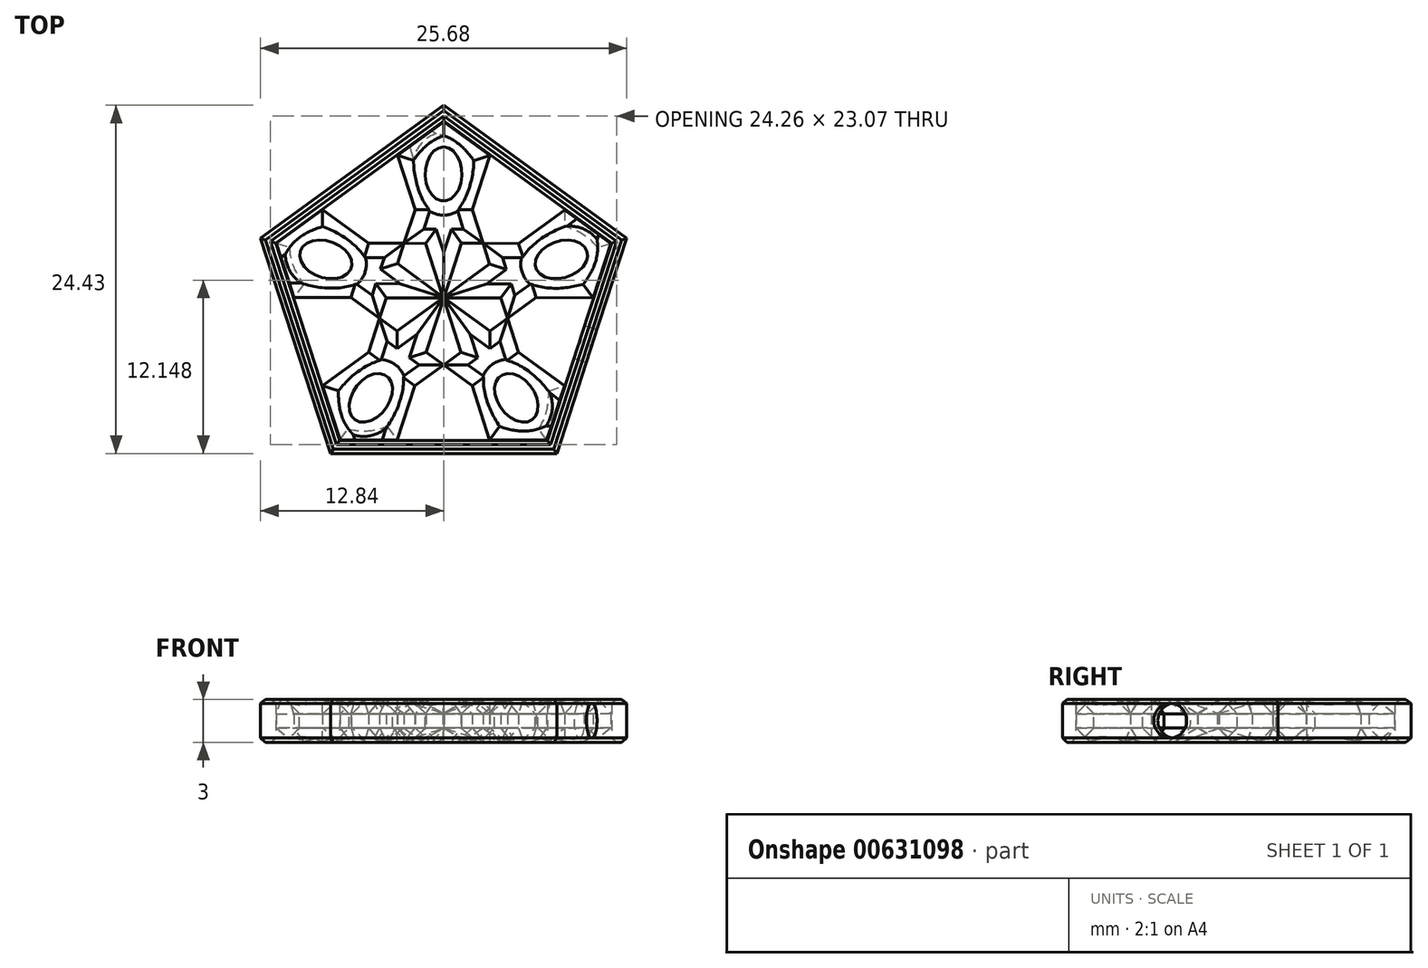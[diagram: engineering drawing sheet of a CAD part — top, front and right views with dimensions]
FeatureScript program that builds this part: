
annotation { "Feature Type Name" : "Feature", "Feature Type Description" : "" }
export const myFeature = defineFeature(function(context is Context, id is Id, definition is map)
    precondition{}
    {
        {
            var Q0;
            Q0=qCreatedBy(makeId("Top.planeOp"),FACE);
            var sketch = newSketch(context, id + "F0", { "sketchPlane" : qUnion([Q0])});
            skCircle(sketch, "E0.cCircle", {"center": v(0, 3.43) * mm, "radius": 2.75 * mm, "construction": true});
            skLineSegment(sketch, "E0.0", {"start": v(-2, 6.18) * mm, "end": v(2, 6.17) * mm});
            skLineSegment(sketch, "E0.1", {"start": v(2, 6.17) * mm, "end": v(3.23, 2.37) * mm});
            skLineSegment(sketch, "E0.2", {"start": v(3.23, 2.37) * mm, "end": v(0, 0.02) * mm});
            skLineSegment(sketch, "E0.3", {"start": v(0, 0.02) * mm, "end": v(-3.24, 2.38) * mm});
            skLineSegment(sketch, "E0.4", {"start": v(-3.24, 2.38) * mm, "end": v(-2, 6.18) * mm});
            skPoint(sketch, "E0.0.midPoint", {"position": v(0, 6.18) * mm});
            skLineSegment(sketch, "E1.MirrorCS", {"start": v(-3.22, 9.99) * mm, "end": v(-2, 6.18) * mm});
            skLineSegment(sketch, "E2.MirrorCS", {"start": v(0.02, 12.33) * mm, "end": v(-3.22, 9.99) * mm});
            skLineSegment(sketch, "E3.MirrorCS", {"start": v(3.25, 9.98) * mm, "end": v(0.02, 12.33) * mm});
            skLineSegment(sketch, "E4.MirrorCS", {"start": v(2, 6.17) * mm, "end": v(3.25, 9.98) * mm});
            skLineSegment(sketch, "E5.1.0", {"start": v(-6.5, 0.01) * mm, "end": v(-5.25, 3.82) * mm});
            skCircle(sketch, "E5.1.1", {"center": v(-3.26, 1.06) * mm, "radius": 2.75 * mm, "construction": true});
            skLineSegment(sketch, "E5.1.2", {"start": v(-5.25, 3.82) * mm, "end": v(-8.48, 6.17) * mm});
            skLineSegment(sketch, "E5.1.3", {"start": v(-11.73, 3.83) * mm, "end": v(-10.5, 0.02) * mm});
            skLineSegment(sketch, "E5.1.4", {"start": v(-3.26, -2.34) * mm, "end": v(-6.5, 0.01) * mm});
            skLineSegment(sketch, "E5.1.5", {"start": v(-0.02, 0) * mm, "end": v(-3.26, -2.34) * mm});
            skLineSegment(sketch, "E5.1.6", {"start": v(-8.48, 6.17) * mm, "end": v(-11.73, 3.83) * mm});
            skLineSegment(sketch, "E5.1.7", {"start": v(-11.73, 3.83) * mm, "end": v(-10.5, 0.02) * mm});
            skLineSegment(sketch, "E5.1.8", {"start": v(-1.25, 3.8) * mm, "end": v(-0.02, 0) * mm});
            skPoint(sketch, "E5.1.9", {"position": v(-5.87, 1.91) * mm});
            skLineSegment(sketch, "E5.1.10", {"start": v(-5.25, 3.82) * mm, "end": v(-1.25, 3.8) * mm});
            skLineSegment(sketch, "E5.1.11", {"start": v(-10.5, 0.02) * mm, "end": v(-6.5, 0.01) * mm});
            skLineSegment(sketch, "E5.2.0", {"start": v(-2.02, -6.17) * mm, "end": v(-5.25, -3.82) * mm});
            skCircle(sketch, "E5.2.1", {"center": v(-2.01, -2.77) * mm, "radius": 2.75 * mm, "construction": true});
            skLineSegment(sketch, "E5.2.2", {"start": v(-5.25, -3.82) * mm, "end": v(-8.5, -6.16) * mm});
            skLineSegment(sketch, "E5.2.3", {"start": v(-7.26, -9.97) * mm, "end": v(-3.26, -9.98) * mm});
            skLineSegment(sketch, "E5.2.4", {"start": v(1.22, -3.83) * mm, "end": v(-2.02, -6.17) * mm});
            skLineSegment(sketch, "E5.2.5", {"start": v(0, -0.02) * mm, "end": v(1.22, -3.83) * mm});
            skLineSegment(sketch, "E5.2.6", {"start": v(-8.5, -6.16) * mm, "end": v(-7.26, -9.97) * mm});
            skLineSegment(sketch, "E5.2.7", {"start": v(-7.26, -9.97) * mm, "end": v(-3.26, -9.98) * mm});
            skLineSegment(sketch, "E5.2.8", {"start": v(-4, -0.02) * mm, "end": v(0, -0.02) * mm});
            skPoint(sketch, "E5.2.9", {"position": v(-3.64, -5) * mm});
            skLineSegment(sketch, "E5.2.10", {"start": v(-5.25, -3.82) * mm, "end": v(-4, -0.02) * mm});
            skLineSegment(sketch, "E5.2.11", {"start": v(-3.26, -9.98) * mm, "end": v(-2.02, -6.17) * mm});
            skLineSegment(sketch, "E5.3.0", {"start": v(5.25, -3.83) * mm, "end": v(2, -6.17) * mm});
            skCircle(sketch, "E5.3.1", {"center": v(2.01, -2.77) * mm, "radius": 2.75 * mm, "construction": true});
            skLineSegment(sketch, "E5.3.2", {"start": v(2, -6.17) * mm, "end": v(3.24, -9.98) * mm});
            skLineSegment(sketch, "E5.3.3", {"start": v(7.24, -9.99) * mm, "end": v(8.48, -6.19) * mm});
            skLineSegment(sketch, "E5.3.4", {"start": v(4.02, -0.02) * mm, "end": v(5.25, -3.83) * mm});
            skLineSegment(sketch, "E5.3.5", {"start": v(0.02, -0.02) * mm, "end": v(4.02, -0.02) * mm});
            skLineSegment(sketch, "E5.3.6", {"start": v(3.24, -9.98) * mm, "end": v(7.24, -9.99) * mm});
            skLineSegment(sketch, "E5.3.7", {"start": v(7.24, -9.99) * mm, "end": v(8.48, -6.19) * mm});
            skLineSegment(sketch, "E5.3.8", {"start": v(-1.22, -3.82) * mm, "end": v(0.02, -0.02) * mm});
            skPoint(sketch, "E5.3.9", {"position": v(3.63, -5) * mm});
            skLineSegment(sketch, "E5.3.10", {"start": v(2, -6.17) * mm, "end": v(-1.22, -3.82) * mm});
            skLineSegment(sketch, "E5.3.11", {"start": v(8.48, -6.19) * mm, "end": v(5.25, -3.83) * mm});
            skLineSegment(sketch, "E5.4.0", {"start": v(5.26, 3.8) * mm, "end": v(6.5, 0) * mm});
            skCircle(sketch, "E5.4.1", {"center": v(3.26, 1.06) * mm, "radius": 2.75 * mm, "construction": true});
            skLineSegment(sketch, "E5.4.2", {"start": v(6.5, 0) * mm, "end": v(10.5, 0) * mm});
            skLineSegment(sketch, "E5.4.3", {"start": v(11.74, 3.8) * mm, "end": v(8.5, 6.15) * mm});
            skLineSegment(sketch, "E5.4.4", {"start": v(1.26, 3.82) * mm, "end": v(5.26, 3.8) * mm});
            skLineSegment(sketch, "E5.4.5", {"start": v(0.02, 0.01) * mm, "end": v(1.26, 3.82) * mm});
            skLineSegment(sketch, "E5.4.6", {"start": v(10.5, 0) * mm, "end": v(11.74, 3.8) * mm});
            skLineSegment(sketch, "E5.4.7", {"start": v(11.74, 3.8) * mm, "end": v(8.5, 6.15) * mm});
            skLineSegment(sketch, "E5.4.8", {"start": v(3.25, -2.34) * mm, "end": v(0.02, 0.01) * mm});
            skPoint(sketch, "E5.4.9", {"position": v(5.88, 1.9) * mm});
            skLineSegment(sketch, "E5.4.10", {"start": v(6.5, 0) * mm, "end": v(3.25, -2.34) * mm});
            skLineSegment(sketch, "E5.4.11", {"start": v(8.5, 6.15) * mm, "end": v(5.26, 3.8) * mm});
            skPoint(sketch, "E5.center", {"position": v(0, 0) * mm});
            skEllipse(sketch, "E6", {"center": v(0, 8.68) * mm, "majorRadius": 1.9 * mm, "minorRadius": 1.29 * mm, "majorAxis": v(0, 1)});
            skEllipse(sketch, "E7.1.1", {"center": v(-8.26, 2.68) * mm, "majorRadius": 1.9 * mm, "minorRadius": 1.29 * mm, "majorAxis": v(-0.95, 0.3)});
            skEllipse(sketch, "E7.2.1", {"center": v(-5.1, -7.02) * mm, "majorRadius": 1.9 * mm, "minorRadius": 1.29 * mm, "majorAxis": v(-0.59, -0.8)});
            skEllipse(sketch, "E7.3.1", {"center": v(5.1, -7.02) * mm, "majorRadius": 1.9 * mm, "minorRadius": 1.29 * mm, "majorAxis": v(0.59, -0.8)});
            skEllipse(sketch, "E7.4.1", {"center": v(8.26, 2.68) * mm, "majorRadius": 1.9 * mm, "minorRadius": 1.29 * mm, "majorAxis": v(0.95, 0.3)});
            skSolve(sketch);
        }
        {
            var Q0;
            {var subQ6=sQuery(id+"F0.wireOp",EDGE,"E0.0");Q0=makeQuery(id+"F0.imprint","IMPRINT",FACE,{"disambiguationData":[TD([[makeQuery(id+"F0.imprint","IMPRINT",EDGE,{"derivedFrom":subQ6}),-1.0]])]});}
            var Q1;
            Q1=makeQuery(id+"F0.imprint","IMPRINT",FACE,{"disambiguationData":[TD([[makeQuery(id+"F0.imprint","IMPRINT",EDGE,{"derivedFrom":sQuery(id+"F0.wireOp",EDGE,"E0.0")}),1.0]])]});
            extrude(context, id + "F1", {"entities" : qUnion([Q0, Q1]), "depth" : 3 * mm, "offsetDistance" : 25 * mm});
        }
        {
            var Q0;
            Q0=makeQuery(id+"F1.opExtrude","CAP_EDGE",EDGE,{"disambiguationData":[OSD([sQuery(id+"F0.wireOp",EDGE,"E5.1.8")])],"isStart":false});
            var Q1;
            Q1=makeQuery(id+"F1.opExtrude","CAP_EDGE",EDGE,{"disambiguationData":[OSD([sQuery(id+"F0.wireOp",EDGE,"E5.1.10")])],"isStart":false});
            var Q2;
            Q2=makeQuery(id+"F1.opExtrude","CAP_EDGE",EDGE,{"disambiguationData":[OSD([sQuery(id+"F0.wireOp",EDGE,"E0.4")])],"isStart":false});
            var Q3;
            Q3=makeQuery(id+"F1.opExtrude","CAP_EDGE",EDGE,{"disambiguationData":[OSD([sQuery(id+"F0.wireOp",EDGE,"E1.MirrorCS")])],"isStart":false});
            var Q4;
            Q4=makeQuery(id+"F1.opExtrude","CAP_EDGE",EDGE,{"disambiguationData":[OSD([sQuery(id+"F0.wireOp",EDGE,"E2.MirrorCS")])],"isStart":false});
            var Q5;
            Q5=makeQuery(id+"F1.opExtrude","CAP_EDGE",EDGE,{"disambiguationData":[OSD([sQuery(id+"F0.wireOp",EDGE,"E3.MirrorCS")])],"isStart":false});
            var Q6;
            Q6=makeQuery(id+"F1.opExtrude","CAP_EDGE",EDGE,{"disambiguationData":[OSD([sQuery(id+"F0.wireOp",EDGE,"E4.MirrorCS")])],"isStart":false});
            var Q7;
            Q7=makeQuery(id+"F1.opExtrude","CAP_EDGE",EDGE,{"disambiguationData":[OSD([sQuery(id+"F0.wireOp",EDGE,"E0.1")])],"isStart":false});
            var Q8;
            Q8=makeQuery(id+"F1.opExtrude","CAP_EDGE",EDGE,{"disambiguationData":[OSD([sQuery(id+"F0.wireOp",EDGE,"E5.4.4")])],"isStart":false});
            var Q9;
            Q9=makeQuery(id+"F1.opExtrude","CAP_FACE",FACE,{"disambiguationData":[OSD([sQuery(id+"F0.wireOp",EDGE,"E0.1"),sQuery(id+"F0.wireOp",EDGE,"E0.2"),sQuery(id+"F0.wireOp",EDGE,"E0.3"),sQuery(id+"F0.wireOp",EDGE,"E0.4"),sQuery(id+"F0.wireOp",EDGE,"E1.MirrorCS"),sQuery(id+"F0.wireOp",EDGE,"E2.MirrorCS"),sQuery(id+"F0.wireOp",EDGE,"E3.MirrorCS"),sQuery(id+"F0.wireOp",EDGE,"E4.MirrorCS"),sQuery(id+"F0.wireOp",EDGE,"E5.1.8"),sQuery(id+"F0.wireOp",EDGE,"E5.1.10"),sQuery(id+"F0.wireOp",EDGE,"E5.4.4"),sQuery(id+"F0.wireOp",EDGE,"E5.4.5"),sQuery(id+"F0.wireOp",EDGE,"E6")])],"isStart":false});
            chamfer(context, id + "F2", {"entities" : qUnion([Q0, Q1, Q2, Q3, Q4, Q5, Q6, Q7, Q8, Q9]), "width" : 1 * mm, "tangentPropagation" : true});
        }
        {
            var Q0;
            Q0=makeQuery(id+"F0.imprint","IMPRINT",FACE,{"disambiguationData":[TD([[makeQuery(id+"F0.imprint","IMPRINT",EDGE,{"derivedFrom":sQuery(id+"F0.wireOp",EDGE,"E5.4.0")}),1.0]])]});
            var Q1;
            {var subQ6=sQuery(id+"F0.wireOp",EDGE,"E5.4.0");Q1=makeQuery(id+"F0.imprint","IMPRINT",FACE,{"disambiguationData":[TD([[makeQuery(id+"F0.imprint","IMPRINT",EDGE,{"derivedFrom":subQ6}),-1.0]])]});}
            extrude(context, id + "F3", {"entities" : qUnion([Q0, Q1]), "depth" : 3 * mm, "offsetDistance" : 25 * mm});
        }
        {
            var Q0;
            Q0=makeQuery(id+"F3.opExtrude","CAP_EDGE",EDGE,{"disambiguationData":[OSD([sQuery(id+"F0.wireOp",EDGE,"E5.3.5")])],"isStart":false});
            var Q1;
            Q1=makeQuery(id+"F3.opExtrude","CAP_EDGE",EDGE,{"disambiguationData":[OSD([sQuery(id+"F0.wireOp",EDGE,"E0.2")])],"isStart":false});
            var Q2;
            Q2=makeQuery(id+"F3.opExtrude","CAP_EDGE",EDGE,{"disambiguationData":[OSD([sQuery(id+"F0.wireOp",EDGE,"E0.1")])],"isStart":false});
            var Q3;
            Q3=makeQuery(id+"F3.opExtrude","CAP_EDGE",EDGE,{"disambiguationData":[OSD([sQuery(id+"F0.wireOp",EDGE,"E5.4.4")])],"isStart":false});
            var Q4;
            Q4=makeQuery(id+"F3.opExtrude","CAP_EDGE",EDGE,{"disambiguationData":[OSD([sQuery(id+"F0.wireOp",EDGE,"E5.4.11")])],"isStart":false});
            var Q5;
            Q5=makeQuery(id+"F3.opExtrude","CAP_EDGE",EDGE,{"disambiguationData":[OSD([sQuery(id+"F0.wireOp",EDGE,"E5.4.3")])],"isStart":false});
            var Q6;
            Q6=makeQuery(id+"F3.opExtrude","CAP_EDGE",EDGE,{"disambiguationData":[OSD([sQuery(id+"F0.wireOp",EDGE,"E5.4.10")])],"isStart":false});
            var Q7;
            Q7=makeQuery(id+"F3.opExtrude","CAP_EDGE",EDGE,{"disambiguationData":[OSD([sQuery(id+"F0.wireOp",EDGE,"E5.3.4")])],"isStart":false});
            var Q8;
            Q8=makeQuery(id+"F3.opExtrude","CAP_EDGE",EDGE,{"disambiguationData":[OSD([sQuery(id+"F0.wireOp",EDGE,"E5.4.2")])],"isStart":false});
            var Q9;
            Q9=makeQuery(id+"F3.opExtrude","CAP_EDGE",EDGE,{"disambiguationData":[OSD([sQuery(id+"F0.wireOp",EDGE,"E5.4.6")])],"isStart":false});
            var Q10;
            Q10=makeQuery(id+"F3.opExtrude","CAP_EDGE",EDGE,{"disambiguationData":[OSD([sQuery(id+"F0.wireOp",EDGE,"E7.4.1")])],"isStart":false});
            chamfer(context, id + "F4", {"entities" : qUnion([Q0, Q1, Q2, Q3, Q4, Q5, Q6, Q7, Q8, Q9, Q10]), "width" : 1 * mm, "tangentPropagation" : true});
        }
        {
            var Q0;
            {var subQ1=sQuery(id+"F0.wireOp",EDGE,"E5.3.0");Q0=makeQuery(id+"F0.imprint","IMPRINT",FACE,{"disambiguationData":[TD([[makeQuery(id+"F0.imprint","IMPRINT",EDGE,{"derivedFrom":subQ1}),-1.0]])]});}
            var Q1;
            Q1=makeQuery(id+"F0.imprint","IMPRINT",FACE,{"disambiguationData":[TD([[makeQuery(id+"F0.imprint","IMPRINT",EDGE,{"derivedFrom":sQuery(id+"F0.wireOp",EDGE,"E5.3.0")}),1.0]])]});
            extrude(context, id + "F5", {"entities" : qUnion([Q0, Q1]), "depth" : 3 * mm, "offsetDistance" : 25 * mm});
        }
        {
            var Q0;
            {var subQ1=sQuery(id+"F0.wireOp",EDGE,"E5.2.0");Q0=makeQuery(id+"F0.imprint","IMPRINT",FACE,{"disambiguationData":[TD([[makeQuery(id+"F0.imprint","IMPRINT",EDGE,{"derivedFrom":subQ1}),-1.0]])]});}
            var Q1;
            Q1=makeQuery(id+"F0.imprint","IMPRINT",FACE,{"disambiguationData":[TD([[makeQuery(id+"F0.imprint","IMPRINT",EDGE,{"derivedFrom":sQuery(id+"F0.wireOp",EDGE,"E5.2.0")}),1.0]])]});
            extrude(context, id + "F6", {"entities" : qUnion([Q0, Q1]), "depth" : 3 * mm, "offsetDistance" : 25 * mm});
        }
        {
            var Q0;
            {var subQ1=sQuery(id+"F0.wireOp",EDGE,"E5.1.0");Q0=makeQuery(id+"F0.imprint","IMPRINT",FACE,{"disambiguationData":[TD([[makeQuery(id+"F0.imprint","IMPRINT",EDGE,{"derivedFrom":subQ1}),-1.0]])]});}
            var Q1;
            Q1=makeQuery(id+"F0.imprint","IMPRINT",FACE,{"disambiguationData":[TD([[makeQuery(id+"F0.imprint","IMPRINT",EDGE,{"derivedFrom":sQuery(id+"F0.wireOp",EDGE,"E5.1.0")}),1.0]])]});
            extrude(context, id + "F7", {"entities" : qUnion([Q0, Q1]), "depth" : 3 * mm, "offsetDistance" : 25 * mm});
        }
        {
            var Q0;
            Q0=makeQuery(id+"F5.opExtrude","CAP_EDGE",EDGE,{"disambiguationData":[OSD([sQuery(id+"F0.wireOp",EDGE,"E5.4.8")])],"isStart":false});
            var Q1;
            Q1=makeQuery(id+"F5.opExtrude","CAP_EDGE",EDGE,{"disambiguationData":[OSD([sQuery(id+"F0.wireOp",EDGE,"E5.4.10")])],"isStart":false});
            var Q2;
            Q2=makeQuery(id+"F5.opExtrude","CAP_EDGE",EDGE,{"disambiguationData":[OSD([sQuery(id+"F0.wireOp",EDGE,"E5.3.4")])],"isStart":false});
            var Q3;
            Q3=makeQuery(id+"F5.opExtrude","CAP_EDGE",EDGE,{"disambiguationData":[OSD([sQuery(id+"F0.wireOp",EDGE,"E5.3.11")])],"isStart":false});
            var Q4;
            Q4=makeQuery(id+"F5.opExtrude","CAP_EDGE",EDGE,{"disambiguationData":[OSD([sQuery(id+"F0.wireOp",EDGE,"E5.3.7")])],"isStart":false});
            var Q5;
            Q5=makeQuery(id+"F5.opExtrude","CAP_EDGE",EDGE,{"disambiguationData":[OSD([sQuery(id+"F0.wireOp",EDGE,"E5.3.6")])],"isStart":false});
            var Q6;
            Q6=makeQuery(id+"F5.opExtrude","CAP_EDGE",EDGE,{"disambiguationData":[OSD([sQuery(id+"F0.wireOp",EDGE,"E5.3.2")])],"isStart":false});
            var Q7;
            Q7=makeQuery(id+"F5.opExtrude","CAP_EDGE",EDGE,{"disambiguationData":[OSD([sQuery(id+"F0.wireOp",EDGE,"E5.3.10")])],"isStart":false});
            var Q8;
            Q8=makeQuery(id+"F5.opExtrude","CAP_EDGE",EDGE,{"disambiguationData":[OSD([sQuery(id+"F0.wireOp",EDGE,"E5.2.4")])],"isStart":false});
            var Q9;
            Q9=makeQuery(id+"F5.opExtrude","CAP_EDGE",EDGE,{"disambiguationData":[OSD([sQuery(id+"F0.wireOp",EDGE,"E5.2.5")])],"isStart":false});
            var Q10;
            Q10=makeQuery(id+"F5.opExtrude","CAP_EDGE",EDGE,{"disambiguationData":[OSD([sQuery(id+"F0.wireOp",EDGE,"E7.3.1")])],"isStart":false});
            chamfer(context, id + "F8", {"entities" : qUnion([Q0, Q1, Q2, Q3, Q4, Q5, Q6, Q7, Q8, Q9, Q10]), "width" : 1 * mm, "tangentPropagation" : true});
        }
        {
            var Q0;
            Q0=makeQuery(id+"F6.opExtrude","CAP_EDGE",EDGE,{"disambiguationData":[OSD([sQuery(id+"F0.wireOp",EDGE,"E7.2.1")])],"isStart":false});
            var Q1;
            Q1=makeQuery(id+"F6.opExtrude","CAP_EDGE",EDGE,{"disambiguationData":[OSD([sQuery(id+"F0.wireOp",EDGE,"E5.2.3")])],"isStart":false});
            var Q2;
            Q2=makeQuery(id+"F6.opExtrude","CAP_EDGE",EDGE,{"disambiguationData":[OSD([sQuery(id+"F0.wireOp",EDGE,"E5.2.6")])],"isStart":false});
            var Q3;
            Q3=makeQuery(id+"F6.opExtrude","CAP_EDGE",EDGE,{"disambiguationData":[OSD([sQuery(id+"F0.wireOp",EDGE,"E5.2.2")])],"isStart":false});
            var Q4;
            Q4=makeQuery(id+"F6.opExtrude","CAP_EDGE",EDGE,{"disambiguationData":[OSD([sQuery(id+"F0.wireOp",EDGE,"E5.2.10")])],"isStart":false});
            var Q5;
            Q5=makeQuery(id+"F6.opExtrude","CAP_EDGE",EDGE,{"disambiguationData":[OSD([sQuery(id+"F0.wireOp",EDGE,"E5.1.4")])],"isStart":false});
            var Q6;
            Q6=makeQuery(id+"F6.opExtrude","CAP_EDGE",EDGE,{"disambiguationData":[OSD([sQuery(id+"F0.wireOp",EDGE,"E5.1.5")])],"isStart":false});
            var Q7;
            Q7=makeQuery(id+"F6.opExtrude","CAP_EDGE",EDGE,{"disambiguationData":[OSD([sQuery(id+"F0.wireOp",EDGE,"E5.3.8")])],"isStart":false});
            var Q8;
            Q8=makeQuery(id+"F6.opExtrude","CAP_EDGE",EDGE,{"disambiguationData":[OSD([sQuery(id+"F0.wireOp",EDGE,"E5.3.10")])],"isStart":false});
            var Q9;
            Q9=makeQuery(id+"F6.opExtrude","CAP_EDGE",EDGE,{"disambiguationData":[OSD([sQuery(id+"F0.wireOp",EDGE,"E5.2.4")])],"isStart":false});
            var Q10;
            Q10=makeQuery(id+"F6.opExtrude","CAP_EDGE",EDGE,{"disambiguationData":[OSD([sQuery(id+"F0.wireOp",EDGE,"E5.2.11")])],"isStart":false});
            chamfer(context, id + "F9", {"entities" : qUnion([Q0, Q1, Q2, Q3, Q4, Q5, Q6, Q7, Q8, Q9, Q10]), "width" : 1 * mm, "tangentPropagation" : true});
        }
        {
            var Q0;
            Q0=makeQuery(id+"F7.opExtrude","CAP_EDGE",EDGE,{"disambiguationData":[OSD([sQuery(id+"F0.wireOp",EDGE,"E5.1.4")])],"isStart":false});
            var Q1;
            Q1=makeQuery(id+"F7.opExtrude","CAP_EDGE",EDGE,{"disambiguationData":[OSD([sQuery(id+"F0.wireOp",EDGE,"E5.2.10")])],"isStart":false});
            var Q2;
            Q2=makeQuery(id+"F7.opExtrude","CAP_EDGE",EDGE,{"disambiguationData":[OSD([sQuery(id+"F0.wireOp",EDGE,"E5.2.8")])],"isStart":false});
            var Q3;
            Q3=makeQuery(id+"F7.opExtrude","CAP_EDGE",EDGE,{"disambiguationData":[OSD([sQuery(id+"F0.wireOp",EDGE,"E0.3")])],"isStart":false});
            var Q4;
            Q4=makeQuery(id+"F7.opExtrude","CAP_EDGE",EDGE,{"disambiguationData":[OSD([sQuery(id+"F0.wireOp",EDGE,"E0.4")])],"isStart":false});
            var Q5;
            Q5=makeQuery(id+"F7.opExtrude","CAP_EDGE",EDGE,{"disambiguationData":[OSD([sQuery(id+"F0.wireOp",EDGE,"E5.1.10")])],"isStart":false});
            var Q6;
            Q6=makeQuery(id+"F7.opExtrude","CAP_EDGE",EDGE,{"disambiguationData":[OSD([sQuery(id+"F0.wireOp",EDGE,"E5.1.2")])],"isStart":false});
            var Q7;
            Q7=makeQuery(id+"F7.opExtrude","CAP_EDGE",EDGE,{"disambiguationData":[OSD([sQuery(id+"F0.wireOp",EDGE,"E5.1.6")])],"isStart":false});
            var Q8;
            Q8=makeQuery(id+"F7.opExtrude","CAP_EDGE",EDGE,{"disambiguationData":[OSD([sQuery(id+"F0.wireOp",EDGE,"E5.1.3")])],"isStart":false});
            var Q9;
            Q9=makeQuery(id+"F7.opExtrude","CAP_EDGE",EDGE,{"disambiguationData":[OSD([sQuery(id+"F0.wireOp",EDGE,"E5.1.11")])],"isStart":false});
            var Q10;
            Q10=makeQuery(id+"F7.opExtrude","CAP_EDGE",EDGE,{"disambiguationData":[OSD([sQuery(id+"F0.wireOp",EDGE,"E7.1.1")])],"isStart":false});
            chamfer(context, id + "F10", {"entities" : qUnion([Q0, Q1, Q2, Q3, Q4, Q5, Q6, Q7, Q8, Q9, Q10]), "width" : 1 * mm, "tangentPropagation" : true});
        }
        {
            var Q0;
            Q0=makeQuery(id+"F1.opExtrude","CAP_EDGE",EDGE,{"disambiguationData":[OSD([sQuery(id+"F0.wireOp",EDGE,"E2.MirrorCS")])],"isStart":true});
            var Q1;
            Q1=makeQuery(id+"F1.opExtrude","CAP_EDGE",EDGE,{"disambiguationData":[OSD([sQuery(id+"F0.wireOp",EDGE,"E3.MirrorCS")])],"isStart":true});
            var Q2;
            Q2=makeQuery(id+"F1.opExtrude","CAP_EDGE",EDGE,{"disambiguationData":[OSD([sQuery(id+"F0.wireOp",EDGE,"E4.MirrorCS")])],"isStart":true});
            var Q3;
            Q3=makeQuery(id+"F1.opExtrude","CAP_EDGE",EDGE,{"disambiguationData":[OSD([sQuery(id+"F0.wireOp",EDGE,"E0.1")])],"isStart":true});
            var Q4;
            Q4=makeQuery(id+"F1.opExtrude","CAP_EDGE",EDGE,{"disambiguationData":[OSD([sQuery(id+"F0.wireOp",EDGE,"E5.4.4")])],"isStart":true});
            var Q5;
            Q5=makeQuery(id+"F1.opExtrude","CAP_EDGE",EDGE,{"disambiguationData":[OSD([sQuery(id+"F0.wireOp",EDGE,"E5.4.5")])],"isStart":true});
            var Q6;
            Q6=makeQuery(id+"F1.opExtrude","CAP_EDGE",EDGE,{"disambiguationData":[OSD([sQuery(id+"F0.wireOp",EDGE,"E5.1.8")])],"isStart":true});
            var Q7;
            Q7=makeQuery(id+"F1.opExtrude","CAP_EDGE",EDGE,{"disambiguationData":[OSD([sQuery(id+"F0.wireOp",EDGE,"E5.1.10")])],"isStart":true});
            var Q8;
            Q8=makeQuery(id+"F1.opExtrude","CAP_EDGE",EDGE,{"disambiguationData":[OSD([sQuery(id+"F0.wireOp",EDGE,"E0.4")])],"isStart":true});
            var Q9;
            Q9=makeQuery(id+"F1.opExtrude","CAP_EDGE",EDGE,{"disambiguationData":[OSD([sQuery(id+"F0.wireOp",EDGE,"E1.MirrorCS")])],"isStart":true});
            var Q10;
            Q10=makeQuery(id+"F1.opExtrude","CAP_EDGE",EDGE,{"disambiguationData":[OSD([sQuery(id+"F0.wireOp",EDGE,"E6")])],"isStart":true});
            chamfer(context, id + "F11", {"entities" : qUnion([Q0, Q1, Q2, Q3, Q4, Q5, Q6, Q7, Q8, Q9, Q10]), "width" : 1 * mm, "tangentPropagation" : true});
        }
        {
            var Q0;
            Q0=makeQuery(id+"F3.opExtrude","CAP_FACE",FACE,{"disambiguationData":[OSD([sQuery(id+"F0.wireOp",EDGE,"E0.1"),sQuery(id+"F0.wireOp",EDGE,"E0.2"),sQuery(id+"F0.wireOp",EDGE,"E5.3.4"),sQuery(id+"F0.wireOp",EDGE,"E5.3.5"),sQuery(id+"F0.wireOp",EDGE,"E5.4.2"),sQuery(id+"F0.wireOp",EDGE,"E5.4.4"),sQuery(id+"F0.wireOp",EDGE,"E5.4.5"),sQuery(id+"F0.wireOp",EDGE,"E5.4.6"),sQuery(id+"F0.wireOp",EDGE,"E5.4.8"),sQuery(id+"F0.wireOp",EDGE,"E5.4.10"),sQuery(id+"F0.wireOp",EDGE,"E5.4.11"),sQuery(id+"F0.wireOp",EDGE,"E5.4.3"),sQuery(id+"F0.wireOp",EDGE,"E7.4.1")])],"isStart":true});
            chamfer(context, id + "F12", {"entities" : qUnion([Q0]), "width" : 1 * mm, "tangentPropagation" : true});
        }
        {
            var Q0;
            Q0=makeQuery(id+"F5.opExtrude","CAP_FACE",FACE,{"disambiguationData":[OSD([sQuery(id+"F0.wireOp",EDGE,"E5.2.4"),sQuery(id+"F0.wireOp",EDGE,"E5.2.5"),sQuery(id+"F0.wireOp",EDGE,"E5.3.2"),sQuery(id+"F0.wireOp",EDGE,"E5.3.4"),sQuery(id+"F0.wireOp",EDGE,"E5.3.5"),sQuery(id+"F0.wireOp",EDGE,"E5.3.6"),sQuery(id+"F0.wireOp",EDGE,"E5.3.7"),sQuery(id+"F0.wireOp",EDGE,"E5.3.8"),sQuery(id+"F0.wireOp",EDGE,"E5.3.10"),sQuery(id+"F0.wireOp",EDGE,"E5.3.11"),sQuery(id+"F0.wireOp",EDGE,"E5.4.8"),sQuery(id+"F0.wireOp",EDGE,"E5.4.10"),sQuery(id+"F0.wireOp",EDGE,"E7.3.1")])],"isStart":true});
            chamfer(context, id + "F13", {"entities" : qUnion([Q0]), "width" : 1 * mm, "tangentPropagation" : true});
        }
        {
            var Q0;
            Q0=makeQuery(id+"F6.opExtrude","CAP_FACE",FACE,{"disambiguationData":[OSD([sQuery(id+"F0.wireOp",EDGE,"E5.1.4"),sQuery(id+"F0.wireOp",EDGE,"E5.1.5"),sQuery(id+"F0.wireOp",EDGE,"E5.2.2"),sQuery(id+"F0.wireOp",EDGE,"E5.2.4"),sQuery(id+"F0.wireOp",EDGE,"E5.2.5"),sQuery(id+"F0.wireOp",EDGE,"E5.2.6"),sQuery(id+"F0.wireOp",EDGE,"E5.2.8"),sQuery(id+"F0.wireOp",EDGE,"E5.2.10"),sQuery(id+"F0.wireOp",EDGE,"E5.2.11"),sQuery(id+"F0.wireOp",EDGE,"E5.3.8"),sQuery(id+"F0.wireOp",EDGE,"E5.3.10"),sQuery(id+"F0.wireOp",EDGE,"E7.2.1"),sQuery(id+"F0.wireOp",EDGE,"E5.2.3")])],"isStart":true});
            chamfer(context, id + "F14", {"entities" : qUnion([Q0]), "width" : 1 * mm, "tangentPropagation" : true});
        }
        {
            var Q0;
            Q0=makeQuery(id+"F7.opExtrude","CAP_FACE",FACE,{"disambiguationData":[OSD([sQuery(id+"F0.wireOp",EDGE,"E0.3"),sQuery(id+"F0.wireOp",EDGE,"E0.4"),sQuery(id+"F0.wireOp",EDGE,"E5.1.2"),sQuery(id+"F0.wireOp",EDGE,"E5.1.4"),sQuery(id+"F0.wireOp",EDGE,"E5.1.5"),sQuery(id+"F0.wireOp",EDGE,"E5.1.6"),sQuery(id+"F0.wireOp",EDGE,"E5.1.8"),sQuery(id+"F0.wireOp",EDGE,"E5.1.10"),sQuery(id+"F0.wireOp",EDGE,"E5.1.11"),sQuery(id+"F0.wireOp",EDGE,"E5.2.8"),sQuery(id+"F0.wireOp",EDGE,"E5.2.10"),sQuery(id+"F0.wireOp",EDGE,"E7.1.1"),sQuery(id+"F0.wireOp",EDGE,"E5.1.3")])],"isStart":true});
            chamfer(context, id + "F15", {"entities" : qUnion([Q0]), "width" : 1 * mm, "tangentPropagation" : true});
        }
        {
            var Q0;
            Q0=qCreatedBy(makeId("Top.planeOp"),FACE);
            var sketch = newSketch(context, id + "F16", { "sketchPlane" : qUnion([Q0])});
            skCircle(sketch, "E8.cCircle", {"center": v(0, 0) * mm, "radius": 10.02 * mm, "construction": true});
            skLineSegment(sketch, "E8.0", {"start": v(-7.28, -10.02) * mm, "end": v(-11.78, 3.83) * mm});
            skLineSegment(sketch, "E8.1", {"start": v(-11.78, 3.83) * mm, "end": v(0, 12.38) * mm});
            skLineSegment(sketch, "E8.2", {"start": v(0, 12.38) * mm, "end": v(11.78, 3.83) * mm});
            skLineSegment(sketch, "E8.3", {"start": v(11.78, 3.83) * mm, "end": v(7.28, -10.02) * mm});
            skLineSegment(sketch, "E8.4", {"start": v(7.28, -10.02) * mm, "end": v(-7.28, -10.02) * mm});
            skPoint(sketch, "E8.0.midPoint", {"position": v(-9.53, -3.1) * mm});
            skCircle(sketch, "E9.cCircle", {"center": v(0, 0) * mm, "radius": 10.93 * mm, "construction": true});
            skLineSegment(sketch, "E9.0", {"start": v(-12.84, 4.17) * mm, "end": v(0, 13.5) * mm});
            skLineSegment(sketch, "E9.1", {"start": v(0, 13.5) * mm, "end": v(12.84, 4.17) * mm});
            skLineSegment(sketch, "E9.2", {"start": v(12.84, 4.17) * mm, "end": v(7.94, -10.93) * mm});
            skLineSegment(sketch, "E9.3", {"start": v(7.94, -10.93) * mm, "end": v(-7.94, -10.93) * mm});
            skLineSegment(sketch, "E9.4", {"start": v(-7.94, -10.93) * mm, "end": v(-12.84, 4.17) * mm});
            skPoint(sketch, "E9.0.midPoint", {"position": v(-6.42, 8.84) * mm});
            skSolve(sketch);
        }
        {
            var Q0;
            Q0=makeQuery(id+"F16.imprint","IMPRINT",FACE,{"disambiguationData":[TD([[makeQuery(id+"F16.imprint","IMPRINT",EDGE,{"derivedFrom":sQuery(id+"F16.wireOp",EDGE,"E8.0")}),1.0]])]});
            extrude(context, id + "F17", {"entities" : qUnion([Q0]), "depth" : 1.5 * mm, "offsetDistance" : 25 * mm});
        }
        {
            var Q0;
            {var subQ6=sQuery(id+"F0.wireOp",EDGE,"E0.0");Q0=makeQuery(id+"F0.imprint","IMPRINT",FACE,{"disambiguationData":[TD([[makeQuery(id+"F0.imprint","IMPRINT",EDGE,{"derivedFrom":subQ6}),-1.0]])]});}
            var Q1;
            Q1=makeQuery(id+"F0.imprint","IMPRINT",FACE,{"disambiguationData":[TD([[makeQuery(id+"F0.imprint","IMPRINT",EDGE,{"derivedFrom":sQuery(id+"F0.wireOp",EDGE,"E0.0")}),1.0]])]});
            extrude(context, id + "F18", {"entities" : qUnion([Q0, Q1]), "depth" : 3 * mm, "offsetDistance" : 25 * mm});
        }
        {
            var Q0;
            Q0=makeQuery(id+"F18.opExtrude","CAP_FACE",FACE,{"disambiguationData":[OSD([sQuery(id+"F0.wireOp",EDGE,"E0.1"),sQuery(id+"F0.wireOp",EDGE,"E0.2"),sQuery(id+"F0.wireOp",EDGE,"E0.3"),sQuery(id+"F0.wireOp",EDGE,"E0.4"),sQuery(id+"F0.wireOp",EDGE,"E1.MirrorCS"),sQuery(id+"F0.wireOp",EDGE,"E3.MirrorCS"),sQuery(id+"F0.wireOp",EDGE,"E4.MirrorCS"),sQuery(id+"F0.wireOp",EDGE,"E5.1.8"),sQuery(id+"F0.wireOp",EDGE,"E5.1.10"),sQuery(id+"F0.wireOp",EDGE,"E5.4.4"),sQuery(id+"F0.wireOp",EDGE,"E5.4.5"),sQuery(id+"F0.wireOp",EDGE,"E6"),sQuery(id+"F0.wireOp",EDGE,"E2.MirrorCS")])],"isStart":false});
            chamfer(context, id + "F19", {"entities" : qUnion([Q0]), "width" : 1 * mm, "tangentPropagation" : true});
        }
        {
            var Q0;
            Q0=makeQuery(id+"F18.opExtrude","CAP_FACE",FACE,{"disambiguationData":[OSD([sQuery(id+"F0.wireOp",EDGE,"E0.1"),sQuery(id+"F0.wireOp",EDGE,"E0.2"),sQuery(id+"F0.wireOp",EDGE,"E0.3"),sQuery(id+"F0.wireOp",EDGE,"E0.4"),sQuery(id+"F0.wireOp",EDGE,"E1.MirrorCS"),sQuery(id+"F0.wireOp",EDGE,"E3.MirrorCS"),sQuery(id+"F0.wireOp",EDGE,"E4.MirrorCS"),sQuery(id+"F0.wireOp",EDGE,"E5.1.8"),sQuery(id+"F0.wireOp",EDGE,"E5.1.10"),sQuery(id+"F0.wireOp",EDGE,"E5.4.4"),sQuery(id+"F0.wireOp",EDGE,"E5.4.5"),sQuery(id+"F0.wireOp",EDGE,"E6"),sQuery(id+"F0.wireOp",EDGE,"E2.MirrorCS")])],"isStart":true});
            chamfer(context, id + "F20", {"entities" : qUnion([Q0]), "width" : 1 * mm, "tangentPropagation" : true});
        }
        {
            var Q0;
            Q0=makeQuery(id+"F17.opExtrude","CAP_FACE",FACE,{"disambiguationData":[OSD([sQuery(id+"F16.wireOp",EDGE,"E8.0"),sQuery(id+"F16.wireOp",EDGE,"E8.1"),sQuery(id+"F16.wireOp",EDGE,"E8.2"),sQuery(id+"F16.wireOp",EDGE,"E8.3"),sQuery(id+"F16.wireOp",EDGE,"E8.4"),sQuery(id+"F16.wireOp",EDGE,"E9.0"),sQuery(id+"F16.wireOp",EDGE,"E9.1"),sQuery(id+"F16.wireOp",EDGE,"E9.2"),sQuery(id+"F16.wireOp",EDGE,"E9.3"),sQuery(id+"F16.wireOp",EDGE,"E9.4")])],"isStart":false});
            extrude(context, id + "F21", {"entities" : qUnion([Q0]), "operationType" : NewBodyOperationType.ADD, "depth" : 1.5 * mm, "offsetDistance" : 25 * mm});
        }
        {
            var Q0;
            Q0=makeQuery(id+"F21.opExtrude","CAP_FACE",FACE,{"disambiguationData":[OSD([sQuery(id+"F16.wireOp",EDGE,"E8.0"),sQuery(id+"F16.wireOp",EDGE,"E8.1"),sQuery(id+"F16.wireOp",EDGE,"E8.2"),sQuery(id+"F16.wireOp",EDGE,"E8.3"),sQuery(id+"F16.wireOp",EDGE,"E8.4"),sQuery(id+"F16.wireOp",EDGE,"E9.0"),sQuery(id+"F16.wireOp",EDGE,"E9.1"),sQuery(id+"F16.wireOp",EDGE,"E9.2"),sQuery(id+"F16.wireOp",EDGE,"E9.3"),sQuery(id+"F16.wireOp",EDGE,"E9.4")])],"isStart":false});
            chamfer(context, id + "F22", {"entities" : qUnion([Q0]), "width" : .3 * mm, "tangentPropagation" : true});
        }
        {
            var Q0;
            Q0=makeQuery(id+"F17.opExtrude","CAP_FACE",FACE,{"disambiguationData":[OSD([sQuery(id+"F16.wireOp",EDGE,"E8.0"),sQuery(id+"F16.wireOp",EDGE,"E8.1"),sQuery(id+"F16.wireOp",EDGE,"E8.2"),sQuery(id+"F16.wireOp",EDGE,"E8.3"),sQuery(id+"F16.wireOp",EDGE,"E8.4"),sQuery(id+"F16.wireOp",EDGE,"E9.0"),sQuery(id+"F16.wireOp",EDGE,"E9.1"),sQuery(id+"F16.wireOp",EDGE,"E9.2"),sQuery(id+"F16.wireOp",EDGE,"E9.3"),sQuery(id+"F16.wireOp",EDGE,"E9.4")])],"isStart":true});
            chamfer(context, id + "F23", {"entities" : qUnion([Q0]), "width" : .3 * mm, "tangentPropagation" : true});
        }
        {
            var Q0;
            {var subQ0=sQuery(id+"F16.wireOp",EDGE,"E9.2");Q0=makeQuery(id+"F21.boolean.opBoolean","MERGE",FACE,{"derivedFrom":[makeQuery(id+"F17.opExtrude","SWEPT_FACE",FACE,{"disambiguationData":[OSD([subQ0])]}),makeQuery(id+"F21.opExtrude","SWEPT_FACE",FACE,{"disambiguationData":[OSD([subQ0])]})]});}
            var sketch = newSketch(context, id + "F24", { "sketchPlane" : qUnion([Q0])});
            skCircle(sketch, "E10", {"center": v(0, 1.52) * mm, "radius": 1.22 * mm});
            skPoint(sketch, "E10.centerSnap0", {"position": v(0, 2.7) * mm});
            skSolve(sketch);
        }
        {
            var Q0;
            Q0 = qSketchRegion(id + "F24", true);
            extrude(context, id + "F25", {"entities" : qUnion([Q0]), "operationType" : NewBodyOperationType.REMOVE, "oppositeDirection" : true, "depth" : 5 * mm, "offsetDistance" : 25 * mm});
        }
    });
